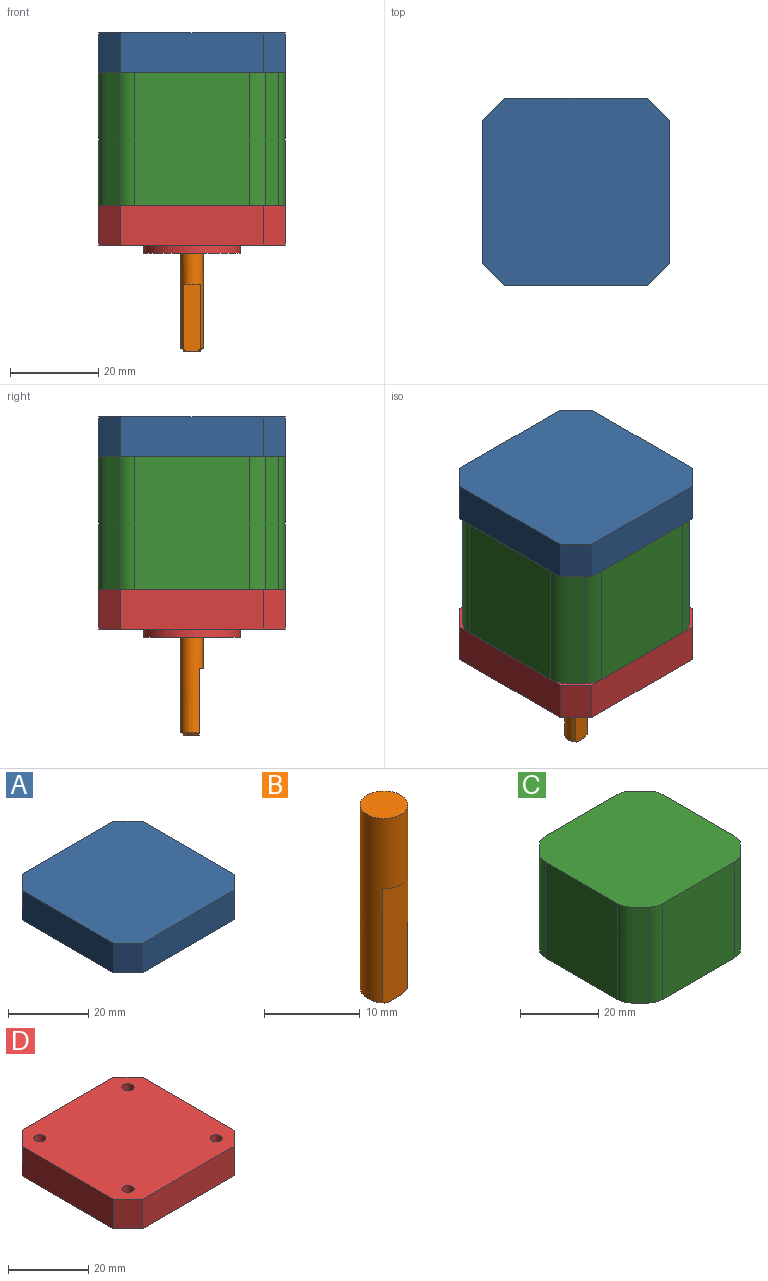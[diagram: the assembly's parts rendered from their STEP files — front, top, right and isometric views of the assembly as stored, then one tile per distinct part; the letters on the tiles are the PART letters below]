
ASSEMBLY  parts=4 mates=3
PART A: 10 faces, bbox 42.3x42.3x9 mm
  f0: plane 32.3x9mm, normal (0,1,0), area 290.7mm2, adj f4,f5,f8,f9
  f1: plane 32.3x9mm, normal (-1,0,0), area 290.7mm2, adj f4,f5,f7,f9
  f2: plane 32.3x9mm, normal (0,-1,0), area 290.7mm2, adj f4,f5,f6,f7
  f3: plane 32.3x9mm, normal (1,0,0), area 290.7mm2, adj f4,f5,f6,f8
  f4: plane 42.3x42.3mm, normal (0,0,1), area 1739.3mm2, adj f0,f1,f2,f3,f6,f7,f8,f9
  f5: plane 42.3x42.3mm, normal (0,0,-1), area 1739.3mm2, adj f0,f1,f2,f3,f6,f7,f8,f9
  f6: plane 9x5mm, normal (0.71,-0.71,0), area 63.6mm2, adj f2,f3,f4,f5
  f7: plane 9x5mm, normal (-0.71,-0.71,0), area 63.6mm2, adj f1,f2,f4,f5
  f8: plane 9x5mm, normal (0.71,0.71,0), area 63.6mm2, adj f0,f3,f4,f5
  f9: plane 9x5mm, normal (-0.71,0.71,0), area 63.6mm2, adj f0,f1,f4,f5
PART B: 6 faces, bbox 5.1x5.1x24.1 mm
  f0: plane 4x3.63mm, normal (0,0,-1), area 12mm2, adj f3,f4
  f1: cylinder r=2.5mm len=23.5mm, axis (0,0,1), area 306.8mm2, adj f2,f3,f4,f5
  f2: plane 5x5mm, normal (0,0,1), area 19.6mm2, adj f1
  f3: cone r=2.5mm half-angle=45deg, axis (0,0,1), area 7.6mm2, adj f0,f1,f4
  f4: plane 15.08x3.87mm, normal (0,-1,0), area 56.5mm2, adj f0,f1,f3,f5
  f5: plane 3.79x0.87mm, normal (0,0,-1), area 2.3mm2, adj f1,f4
PART C: 18 faces, bbox 42.3x42.3x30 mm
  f0: plane 30x26.16mm, normal (-1,0,0), area 784.7mm2, adj f4,f5,f12,f13
  f1: plane 30x26.16mm, normal (0,-1,0), area 784.7mm2, adj f4,f5,f14,f15
  f2: plane 30x26.16mm, normal (1,0,0), area 784.7mm2, adj f4,f5,f16,f17
  f3: plane 30x26.16mm, normal (0,1,0), area 784.7mm2, adj f4,f5,f10,f11
  f4: plane 42.3x42.3mm, normal (0,0,1), area 1713mm2, adj f0,f1,f2,f3,f6,f7,f8,f9
  f5: plane 42.3x42.3mm, normal (0,0,-1), area 1713mm2, adj f0,f1,f2,f3,f6,f7,f8,f9
  f6: plane 30x3.07mm, normal (0.71,-0.71,0), area 130.3mm2, adj f4,f5,f14,f16
  f7: plane 30x3.07mm, normal (-0.71,-0.71,0), area 130.3mm2, adj f4,f5,f12,f15
  f8: plane 30x3.07mm, normal (0.71,0.71,0), area 130.3mm2, adj f4,f5,f10,f17
  f9: plane 30x3.07mm, normal (-0.71,0.71,0), area 130.3mm2, adj f4,f5,f11,f13
  f10: cylinder r=5mm len=30mm, axis (0,0,1), area 117.8mm2, adj f3,f4,f5,f8
  f11: cylinder r=5mm len=30mm, axis (0,0,1), area 117.8mm2, adj f3,f4,f5,f9
  f12: cylinder r=5mm len=30mm, axis (0,0,1), area 117.8mm2, adj f0,f4,f5,f7
  f13: cylinder r=5mm len=30mm, axis (0,0,-1), area 117.8mm2, adj f0,f4,f5,f9
  f14: cylinder r=5mm len=30mm, axis (0,0,-1), area 117.8mm2, adj f1,f4,f5,f6
  f15: cylinder r=5mm len=30mm, axis (0,0,-1), area 117.8mm2, adj f1,f4,f5,f7
  f16: cylinder r=5mm len=30mm, axis (0,0,-1), area 117.8mm2, adj f2,f4,f5,f6
  f17: cylinder r=5mm len=30mm, axis (0,0,1), area 117.8mm2, adj f2,f4,f5,f8
PART D: 18 faces, bbox 42.3x42.3x10.9 mm
  f0: plane 32.3x9mm, normal (0,1,0), area 290.7mm2, adj f8,f9,f11,f13
  f1: plane 32.3x9mm, normal (-1,0,0), area 290.7mm2, adj f8,f9,f12,f13
  f2: plane 32.3x9mm, normal (0,-1,0), area 290.7mm2, adj f8,f9,f10,f12
  f3: cylinder r=1.5mm len=9mm, axis (0,0,-1), area 84.8mm2, adj f8,f9
  f4: cylinder r=1.5mm len=9mm, axis (0,0,-1), area 84.8mm2, adj f8,f9
  f5: cylinder r=1.5mm len=9mm, axis (0,0,-1), area 84.8mm2, adj f8,f9
  f6: cylinder r=1.5mm len=9mm, axis (0,0,-1), area 84.8mm2, adj f8,f9
  f7: plane 32.3x9mm, normal (1,0,0), area 290.7mm2, adj f8,f9,f10,f11
  f8: plane 42.3x42.3mm, normal (0,0,1), area 1711mm2, adj f0,f1,f2,f3,f4,f5,f6,f7
  f9: plane 42.3x42.3mm, normal (0,0,-1), area 1332.6mm2, adj f0,f1,f2,f3,f4,f5,f6,f7
  f10: plane 9x5mm, normal (0.71,-0.71,0), area 63.6mm2, adj f2,f7,f8,f9
  f11: plane 9x5mm, normal (0.71,0.71,0), area 63.6mm2, adj f0,f7,f8,f9
  f12: plane 9x5mm, normal (-0.71,-0.71,0), area 63.6mm2, adj f1,f2,f8,f9
  f13: plane 9x5mm, normal (-0.71,0.71,0), area 63.6mm2, adj f0,f1,f8,f9
  f14: cylinder r=4.5mm len=9mm, axis (0,0,1), area 52.3mm2, adj f16,f17
  f15: cylinder r=10.97mm len=21.95mm, axis (0,0,1), area 127.6mm2, adj f9,f16
  f16: plane 21.95x21.95mm, normal (0,0,-1), area 314.8mm2, adj f14,f15
  f17: plane 9x9mm, normal (0,0,-1), area 63.6mm2, adj f14
PLACE A t=(2.01,-1.47,-16.57)mm
PLACE B t=(2.01,-1.47,-16.57)mm
PLACE C t=(2.01,-1.47,-16.57)mm
PLACE D t=(2.01,-1.47,-16.57)mm
MATE fastened C.f5 <-> D.f14  axis (0,0,-1) through (2.01,-1.47,-7.57)mm
MATE fastened A.f5 <-> C.f4  axis (0,0,-1) through (2.01,-1.47,22.43)mm
MATE revolute D.f14 <-> B.f1  axis (0,0,-1) through (2.01,-1.47,-16.57)mm
